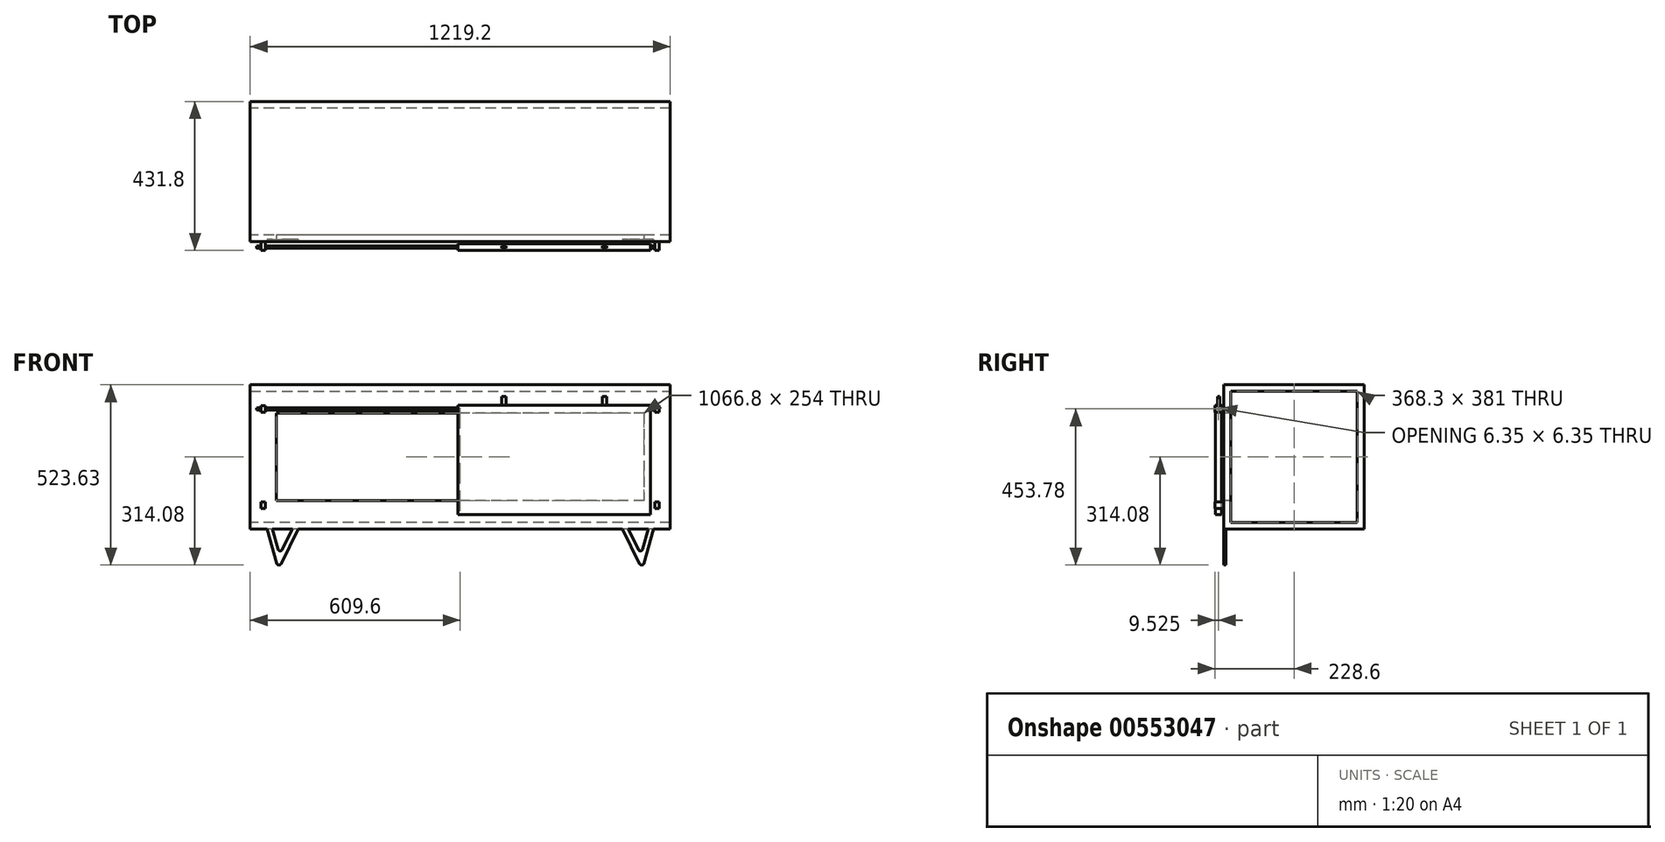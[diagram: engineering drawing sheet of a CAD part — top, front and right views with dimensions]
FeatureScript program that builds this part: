
annotation { "Feature Type Name" : "Feature", "Feature Type Description" : "" }
export const myFeature = defineFeature(function(context is Context, id is Id, definition is map)
    precondition{}
    {
        {
            var Q0;
            Q0=qCreatedBy(makeId("Top.planeOp"),FACE);
            var sketch = newSketch(context, id + "F0", { "sketchPlane" : qUnion([Q0])});
            skLineSegment(sketch, "E0.bottom", {"start": v(609.6, 203.2) * mm, "end": v(-609.6, 203.2) * mm});
            skLineSegment(sketch, "E0.top", {"start": v(609.6, -203.2) * mm, "end": v(-609.6, -203.2) * mm});
            skLineSegment(sketch, "E0.left", {"start": v(609.6, 203.2) * mm, "end": v(609.6, -203.2) * mm});
            skLineSegment(sketch, "E0.right", {"start": v(-609.6, 203.2) * mm, "end": v(-609.6, -203.2) * mm});
            skPoint(sketch, "E0.middle", {"position": v(0, 0) * mm});
            skSolve(sketch);
        }
        {
            var Q0;
            Q0 = qSketchRegion(id + "F0", true);
            extrude(context, id + "F1", {"entities" : qUnion([Q0]), "depth" : 19.05 * mm, "offsetDistance" : 25.4 * mm});
        }
        {
            var Q0;
            Q0=makeQuery(id+"F1.opExtrude","SWEPT_FACE",FACE,{"disambiguationData":[OSD([sQuery(id+"F0.wireOp",EDGE,"E0.top")])]});
            var sketch = newSketch(context, id + "F2", { "sketchPlane" : qUnion([Q0])});
            skLineSegment(sketch, "E1.bottom", {"start": v(-609.6, 19.05) * mm, "end": v(609.6, 19.05) * mm});
            skLineSegment(sketch, "E1.top", {"start": v(-609.6, 400.05) * mm, "end": v(609.6, 400.05) * mm});
            skLineSegment(sketch, "E1.left", {"start": v(-609.6, 19.05) * mm, "end": v(-609.6, 400.05) * mm});
            skLineSegment(sketch, "E1.right", {"start": v(609.6, 19.05) * mm, "end": v(609.6, 400.05) * mm});
            skLineSegment(sketch, "E2.bottom", {"start": v(533.4, 336.55) * mm, "end": v(-533.4, 336.55) * mm});
            skLineSegment(sketch, "E2.top", {"start": v(533.4, 82.55) * mm, "end": v(-533.4, 82.55) * mm});
            skLineSegment(sketch, "E2.left", {"start": v(533.4, 336.55) * mm, "end": v(533.4, 82.55) * mm});
            skLineSegment(sketch, "E2.right", {"start": v(-533.4, 336.55) * mm, "end": v(-533.4, 82.55) * mm});
            skPoint(sketch, "E2.middle", {"position": v(0, 209.55) * mm});
            skPoint(sketch, "E2.middle.positionSnap0", {"position": v(-609.6, 209.55) * mm});
            skPoint(sketch, "E2.centerSnap0", {"position": v(-609.6, 209.55) * mm});
            skLineSegment(sketch, "E3", {"start": v(-533.4, 209.55) * mm, "end": v(-561.9, 209.55) * mm});
            skSolve(sketch);
        }
        {
            var Q0;
            Q0=makeQuery(id+"F2.imprint","IMPRINT",FACE,{"disambiguationData":[TD([[makeQuery(id+"F2.imprint","IMPRINT",EDGE,{"derivedFrom":sQuery(id+"F2.wireOp",EDGE,"E1.bottom")}),-1.0]])]});
            extrude(context, id + "F3", {"entities" : qUnion([Q0]), "operationType" : NewBodyOperationType.ADD, "oppositeDirection" : true, "depth" : 19.05 * mm, "offsetDistance" : 25.4 * mm});
        }
        {
            var Q0;
            Q0=makeQuery(id+"F1.opExtrude","SWEPT_FACE",FACE,{"disambiguationData":[OSD([sQuery(id+"F0.wireOp",EDGE,"E0.bottom")])]});
            var sketch = newSketch(context, id + "F4", { "sketchPlane" : qUnion([Q0])});
            skLineSegment(sketch, "E4.bottom", {"start": v(-609.6, 19.05) * mm, "end": v(609.6, 19.05) * mm});
            skLineSegment(sketch, "E4.top", {"start": v(-609.6, 400.05) * mm, "end": v(609.6, 400.05) * mm});
            skLineSegment(sketch, "E4.left", {"start": v(-609.6, 19.05) * mm, "end": v(-609.6, 400.05) * mm});
            skLineSegment(sketch, "E4.right", {"start": v(609.6, 19.05) * mm, "end": v(609.6, 400.05) * mm});
            skSolve(sketch);
        }
        {
            var Q0;
            Q0=makeQuery(id+"F4.imprint","IMPRINT",FACE,{"disambiguationData":[TD([[makeQuery(id+"F4.imprint","IMPRINT",EDGE,{"derivedFrom":sQuery(id+"F4.wireOp",EDGE,"E4.bottom")}),1.0]])]});
            extrude(context, id + "F5", {"entities" : qUnion([Q0]), "operationType" : NewBodyOperationType.ADD, "oppositeDirection" : true, "depth" : 19.05 * mm, "offsetDistance" : 25.4 * mm});
        }
        {
            var Q0;
            Q0=makeQuery(id+"F5.opExtrude","SWEPT_FACE",FACE,{"disambiguationData":[OSD([sQuery(id+"F4.wireOp",EDGE,"E4.top")])]});
            var sketch = newSketch(context, id + "F6", { "sketchPlane" : qUnion([Q0])});
            skLineSegment(sketch, "E5.bottom", {"start": v(-609.6, 203.2) * mm, "end": v(609.6, 203.2) * mm});
            skLineSegment(sketch, "E5.top", {"start": v(-609.6, -203.2) * mm, "end": v(609.6, -203.2) * mm});
            skLineSegment(sketch, "E5.left", {"start": v(-609.6, 203.2) * mm, "end": v(-609.6, -203.2) * mm});
            skLineSegment(sketch, "E5.right", {"start": v(609.6, 203.2) * mm, "end": v(609.6, -203.2) * mm});
            skSolve(sketch);
        }
        {
            var Q0;
            Q0 = qSketchRegion(id + "F6", true);
            extrude(context, id + "F7", {"entities" : qUnion([Q0]), "operationType" : NewBodyOperationType.ADD, "depth" : 19.05 * mm, "offsetDistance" : 25.4 * mm});
        }
        {
            var Q0;
            Q0=makeQuery(id+"F7.boolean.opBoolean","MERGE",FACE,{"derivedFrom":[makeQuery(id+"F3.boolean.opBoolean","MERGE",FACE,{"derivedFrom":[makeQuery(id+"F1.opExtrude","SWEPT_FACE",FACE,{"disambiguationData":[OSD([sQuery(id+"F0.wireOp",EDGE,"E0.top")])]}),makeQuery(id+"F3.opExtrude","CAP_FACE",FACE,{"disambiguationData":[OSD([sQuery(id+"F2.wireOp",EDGE,"E1.bottom"),sQuery(id+"F2.wireOp",EDGE,"E1.top"),sQuery(id+"F2.wireOp",EDGE,"E1.left"),sQuery(id+"F2.wireOp",EDGE,"E1.right"),sQuery(id+"F2.wireOp",EDGE,"E2.bottom"),sQuery(id+"F2.wireOp",EDGE,"E2.top"),sQuery(id+"F2.wireOp",EDGE,"E2.left"),sQuery(id+"F2.wireOp",EDGE,"E2.right")])],"isStart":true})]}),makeQuery(id+"F7.opExtrude","SWEPT_FACE",FACE,{"disambiguationData":[OSD([sQuery(id+"F6.wireOp",EDGE,"E5.top")])]})]});
            var sketch = newSketch(context, id + "F8", { "sketchPlane" : qUnion([Q0])});
            skLineSegment(sketch, "E6.bottom", {"start": v(-577.85, 358.77) * mm, "end": v(-565.15, 358.77) * mm});
            skLineSegment(sketch, "E6.top", {"start": v(-577.85, 339.72) * mm, "end": v(-565.15, 339.72) * mm});
            skLineSegment(sketch, "E6.left", {"start": v(-577.85, 358.78) * mm, "end": v(-577.85, 339.73) * mm});
            skLineSegment(sketch, "E6.right", {"start": v(-565.15, 358.77) * mm, "end": v(-565.15, 339.73) * mm});
            skPoint(sketch, "E6.middle", {"position": v(-571.5, 349.25) * mm});
            skLineSegment(sketch, "E7.MirrorCS", {"start": v(577.85, 358.78) * mm, "end": v(577.85, 339.73) * mm});
            skLineSegment(sketch, "E8.MirrorCS", {"start": v(577.85, 358.77) * mm, "end": v(565.15, 358.77) * mm});
            skLineSegment(sketch, "E9.MirrorCS", {"start": v(565.15, 358.77) * mm, "end": v(565.15, 339.72) * mm});
            skLineSegment(sketch, "E10.MirrorCS", {"start": v(577.85, 339.72) * mm, "end": v(565.15, 339.72) * mm});
            skLineSegment(sketch, "E11", {"start": v(-609.6, 209.55) * mm, "end": v(-671.65, 209.55) * mm});
            skLineSegment(sketch, "E12.MirrorCS", {"start": v(-565.15, 60.33) * mm, "end": v(-565.15, 79.38) * mm});
            skLineSegment(sketch, "E13.MirrorCS", {"start": v(-577.85, 60.33) * mm, "end": v(-565.15, 60.33) * mm});
            skLineSegment(sketch, "E14.MirrorCS", {"start": v(-577.85, 60.33) * mm, "end": v(-577.85, 79.38) * mm});
            skLineSegment(sketch, "E15.MirrorCS", {"start": v(-577.85, 79.38) * mm, "end": v(-565.15, 79.38) * mm});
            skLineSegment(sketch, "E16.MirrorCS", {"start": v(577.85, 60.33) * mm, "end": v(565.15, 60.33) * mm});
            skLineSegment(sketch, "E17.MirrorCS", {"start": v(565.15, 60.33) * mm, "end": v(565.15, 79.38) * mm});
            skLineSegment(sketch, "E18.MirrorCS", {"start": v(577.85, 60.33) * mm, "end": v(577.85, 79.38) * mm});
            skLineSegment(sketch, "E19.MirrorCS", {"start": v(577.85, 79.38) * mm, "end": v(565.15, 79.38) * mm});
            skSolve(sketch);
        }
        {
            var Q0;
            Q0 = qSketchRegion(id + "F8", true);
            extrude(context, id + "F9", {"entities" : qUnion([Q0]), "operationType" : NewBodyOperationType.ADD, "depth" : 25.4 * mm, "offsetDistance" : 25.4 * mm});
        }
        {
            var Q0;
            Q0=makeQuery(id+"F9.opExtrude","SWEPT_FACE",FACE,{"disambiguationData":[OSD([sQuery(id+"F8.wireOp",EDGE,"E7.MirrorCS")])]});
            var sketch = newSketch(context, id + "F10", { "sketchPlane" : qUnion([Q0])});
            skCircle(sketch, "E20", {"center": v(-219.08, 349.25) * mm, "radius": 3.18 * mm});
            skPoint(sketch, "E20.centerSnap0", {"position": v(-228.6, 349.25) * mm});
            skCircle(sketch, "E21", {"center": v(-219.08, 12.7) * mm, "radius": 3.18 * mm});
            skSolve(sketch);
        }
        {
            var Q0;
            Q0=makeQuery(id+"F10.imprint","IMPRINT",FACE,{"disambiguationData":[TD([[makeQuery(id+"F10.imprint","IMPRINT",EDGE,{"derivedFrom":sQuery(id+"F10.wireOp",EDGE,"E20")}),1.0]])]});
            extrude(context, id + "F11", {"entities" : qUnion([Q0]), "operationType" : NewBodyOperationType.ADD, "oppositeDirection" : true, "depth" : 1168.4 * mm, "offsetDistance" : 25.4 * mm});
        }
        {
            var Q0;
            Q0=makeQuery(id+"F7.boolean.opBoolean","MERGE",FACE,{"derivedFrom":[makeQuery(id+"F3.boolean.opBoolean","MERGE",FACE,{"derivedFrom":[makeQuery(id+"F1.opExtrude","SWEPT_FACE",FACE,{"disambiguationData":[OSD([sQuery(id+"F0.wireOp",EDGE,"E0.top")])]}),makeQuery(id+"F3.opExtrude","CAP_FACE",FACE,{"disambiguationData":[OSD([sQuery(id+"F2.wireOp",EDGE,"E1.bottom"),sQuery(id+"F2.wireOp",EDGE,"E1.top"),sQuery(id+"F2.wireOp",EDGE,"E1.left"),sQuery(id+"F2.wireOp",EDGE,"E1.right"),sQuery(id+"F2.wireOp",EDGE,"E2.bottom"),sQuery(id+"F2.wireOp",EDGE,"E2.top"),sQuery(id+"F2.wireOp",EDGE,"E2.left"),sQuery(id+"F2.wireOp",EDGE,"E2.right")])],"isStart":true})]}),makeQuery(id+"F7.opExtrude","SWEPT_FACE",FACE,{"disambiguationData":[OSD([sQuery(id+"F6.wireOp",EDGE,"E5.top")])]})]});
            cPlane(context, id + "F12", {"entities" : qUnion([Q0]), "cplaneType" : CPlaneType.OFFSET, "offset" : 15.88 * mm, "width" : 152.4 * mm, "height" : 152.4 * mm});
        }
        {
            var Q0;
            Q0=qCreatedBy(id+"F12.planeOp",FACE);
            var sketch = newSketch(context, id + "F13", { "sketchPlane" : qUnion([Q0])});
            skLineSegment(sketch, "E22.bottom", {"start": v(552.45, 41.91) * mm, "end": v(-6.35, 41.9) * mm});
            skLineSegment(sketch, "E22.top", {"start": v(552.45, 359.41) * mm, "end": v(-6.35, 359.4) * mm});
            skLineSegment(sketch, "E22.left", {"start": v(552.45, 41.91) * mm, "end": v(552.45, 359.41) * mm});
            skLineSegment(sketch, "E22.right", {"start": v(-6.35, 41.9) * mm, "end": v(-6.35, 359.4) * mm});
            skPoint(sketch, "E22.middle", {"position": v(273.05, 200.66) * mm});
            skSolve(sketch);
        }
        {
            var Q0;
            Q0=makeQuery(id+"F13.imprint","IMPRINT",FACE,{"disambiguationData":[TD([[makeQuery(id+"F13.imprint","IMPRINT",EDGE,{"derivedFrom":sQuery(id+"F13.wireOp",EDGE,"E22.bottom")}),-1.0]])]});
            extrude(context, id + "F14", {"entities" : qUnion([Q0]), "depth" : 9.4 * mm, "offsetDistance" : 25.4 * mm});
        }
        {
            var Q0;
            Q0 = qSketchRegion(id + "F13", true);
            extrude(context, id + "F15", {"entities" : qUnion([Q0]), "operationType" : NewBodyOperationType.ADD, "oppositeDirection" : true, "depth" : 9.4 * mm, "offsetDistance" : 25.4 * mm});
        }
        {
            var Q0;
            Q0=qCreatedBy(id+"F12.planeOp",FACE);
            var sketch = newSketch(context, id + "F16", { "sketchPlane" : qUnion([Q0])});
            skLineSegment(sketch, "E23.bottom", {"start": v(120.65, 360.26) * mm, "end": v(133.35, 360.26) * mm});
            skLineSegment(sketch, "E23.top", {"start": v(120.65, 385.66) * mm, "end": v(133.35, 385.66) * mm});
            skLineSegment(sketch, "E23.left", {"start": v(120.65, 360.26) * mm, "end": v(120.65, 385.66) * mm});
            skLineSegment(sketch, "E23.right", {"start": v(133.35, 360.26) * mm, "end": v(133.35, 385.66) * mm});
            skLineSegment(sketch, "E24.bottom", {"start": v(412.75, 360.26) * mm, "end": v(425.45, 360.26) * mm});
            skLineSegment(sketch, "E24.top", {"start": v(412.75, 385.66) * mm, "end": v(425.45, 385.66) * mm});
            skLineSegment(sketch, "E24.left", {"start": v(412.75, 360.26) * mm, "end": v(412.75, 385.66) * mm});
            skLineSegment(sketch, "E24.right", {"start": v(425.45, 360.26) * mm, "end": v(425.45, 385.66) * mm});
            skSolve(sketch);
        }
        {
            var Q0;
            Q0 = qSketchRegion(id + "F16", true);
            extrude(context, id + "F17", {"entities" : qUnion([Q0]), "operationType" : NewBodyOperationType.ADD, "depth" : 3.17 * mm, "offsetDistance" : 25.4 * mm});
        }
        {
            var Q0;
            Q0 = qSketchRegion(id + "F16", true);
            extrude(context, id + "F18", {"entities" : qUnion([Q0]), "operationType" : NewBodyOperationType.ADD, "oppositeDirection" : true, "depth" : 3.17 * mm, "offsetDistance" : 25.4 * mm});
        }
        {
            var Q0;
            Q0=makeQuery(id+"F7.boolean.opBoolean","MERGE",FACE,{"derivedFrom":[makeQuery(id+"F3.boolean.opBoolean","MERGE",FACE,{"derivedFrom":[makeQuery(id+"F1.opExtrude","SWEPT_FACE",FACE,{"disambiguationData":[OSD([sQuery(id+"F0.wireOp",EDGE,"E0.top")])]}),makeQuery(id+"F3.opExtrude","CAP_FACE",FACE,{"disambiguationData":[OSD([sQuery(id+"F2.wireOp",EDGE,"E1.bottom"),sQuery(id+"F2.wireOp",EDGE,"E1.top"),sQuery(id+"F2.wireOp",EDGE,"E1.left"),sQuery(id+"F2.wireOp",EDGE,"E1.right"),sQuery(id+"F2.wireOp",EDGE,"E2.bottom"),sQuery(id+"F2.wireOp",EDGE,"E2.top"),sQuery(id+"F2.wireOp",EDGE,"E2.left"),sQuery(id+"F2.wireOp",EDGE,"E2.right")])],"isStart":true})]}),makeQuery(id+"F7.opExtrude","SWEPT_FACE",FACE,{"disambiguationData":[OSD([sQuery(id+"F6.wireOp",EDGE,"E5.top")])]})]});
            var sketch = newSketch(context, id + "F19", { "sketchPlane" : qUnion([Q0])});
            skLineSegment(sketch, "E25", {"start": v(-560.47, 0) * mm, "end": v(-532.4, -99.9) * mm});
            skLineSegment(sketch, "E26", {"start": v(-520.6, -101) * mm, "end": v(-470.64, 0) * mm});
            skArc(sketch, "E27.filletArc", {"start": v(-532.4, -99.9) * mm, "mid": v(-526.88, -104.5) * mm, "end": v(-520.6, -101) * mm});
            skLineSegment(sketch, "E28", {"start": v(-545.34, 0) * mm, "end": v(-528.83, -58.76) * mm});
            skLineSegment(sketch, "E29", {"start": v(-487.41, 0) * mm, "end": v(-517.02, -59.85) * mm});
            skPoint(sketch, "E30.visualSharp", {"position": v(-524.35, -74.67) * mm});
            skArc(sketch, "E30.filletArc", {"start": v(-528.83, -58.76) * mm, "mid": v(-523.3, -63.36) * mm, "end": v(-517.02, -59.85) * mm});
            skLineSegment(sketch, "E31.MirrorCS", {"start": v(560.47, 0) * mm, "end": v(532.4, -99.9) * mm});
            skLineSegment(sketch, "E32.MirrorCS", {"start": v(545.34, 0) * mm, "end": v(528.83, -58.76) * mm});
            skLineSegment(sketch, "E33.MirrorCS", {"start": v(520.6, -101) * mm, "end": v(470.64, 0) * mm});
            skLineSegment(sketch, "E34.MirrorCS", {"start": v(487.41, 0) * mm, "end": v(517.02, -59.85) * mm});
            skArc(sketch, "E35.MirrorCS", {"start": v(528.83, -58.76) * mm, "mid": v(523.3, -63.36) * mm, "end": v(517.02, -59.85) * mm});
            skArc(sketch, "E36.MirrorCS", {"start": v(532.4, -99.9) * mm, "mid": v(526.88, -104.5) * mm, "end": v(520.6, -101) * mm});
            skLineSegment(sketch, "E37", {"start": v(470.64, 0) * mm, "end": v(487.41, 0) * mm});
            skLineSegment(sketch, "E38", {"start": v(545.34, 0) * mm, "end": v(560.47, 0) * mm});
            skSolve(sketch);
        }
        {
            var Q0;
            Q0 = qSketchRegion(id + "F19", true);
            var Q1;
            {var subQ2=sQuery(id+"F19.wireOp",EDGE,"E25");Q1=makeQuery(id+"F19.imprint","IMPRINT",FACE,{"disambiguationData":[TD([[makeQuery(id+"F19.imprint","IMPRINT",EDGE,{"derivedFrom":subQ2}),1.0]])]});}
            extrude(context, id + "F20", {"entities" : qUnion([Q0, Q1]), "operationType" : NewBodyOperationType.ADD, "oppositeDirection" : true, "depth" : 6.35 * mm, "offsetDistance" : 25.4 * mm});
        }
    });
